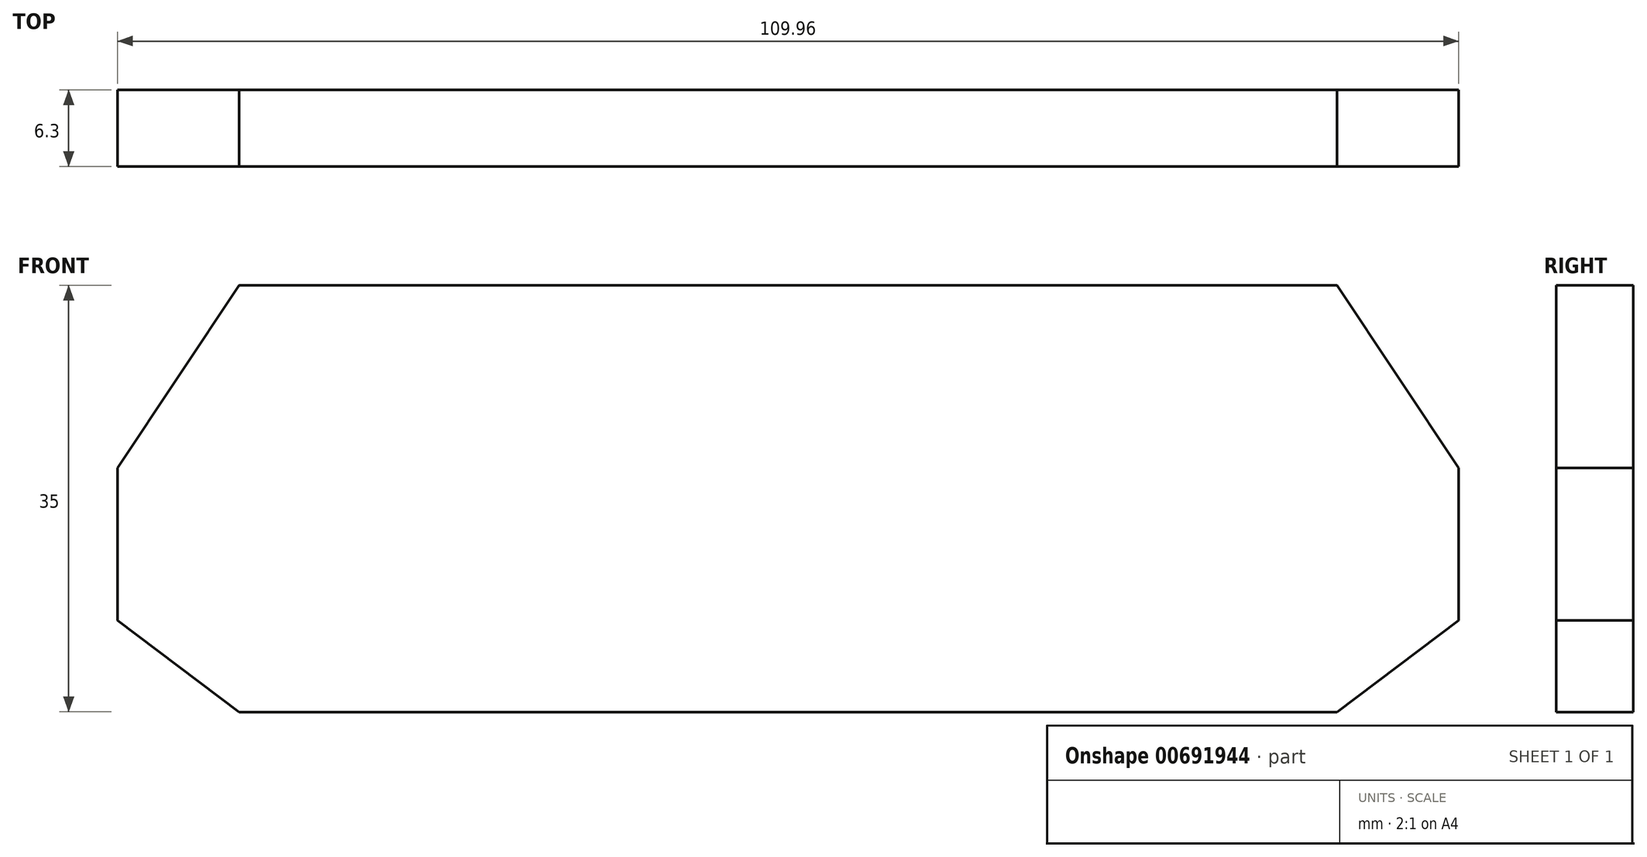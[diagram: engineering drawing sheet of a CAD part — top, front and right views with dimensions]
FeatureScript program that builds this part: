
annotation { "Feature Type Name" : "Feature", "Feature Type Description" : "" }
export const myFeature = defineFeature(function(context is Context, id is Id, definition is map)
    precondition{}
    {
        {
            var Q0;
            Q0=qCreatedBy(makeId("Front.planeOp"),FACE);
            var sketch = newSketch(context, id + "F0", { "sketchPlane" : qUnion([Q0])});
            skLineSegment(sketch, "E0", {"start": v(45, 48.44) * mm, "end": v(54.98, 33.46) * mm});
            skLineSegment(sketch, "E1", {"start": v(54.98, 33.46) * mm, "end": v(54.98, 20.96) * mm});
            skLineSegment(sketch, "E2", {"start": v(54.98, 20.96) * mm, "end": v(45, 13.44) * mm});
            skLineSegment(sketch, "E3", {"start": v(45, 13.44) * mm, "end": v(0, 13.44) * mm});
            skLineSegment(sketch, "E4", {"start": v(45, 48.44) * mm, "end": v(0, 48.44) * mm});
            skLineSegment(sketch, "E5", {"start": v(0, 48.44) * mm, "end": v(0, 13.44) * mm});
            skLineSegment(sketch, "E6.MirrorCS", {"start": v(-45, 48.44) * mm, "end": v(0, 48.44) * mm});
            skLineSegment(sketch, "E7.MirrorCS", {"start": v(-45, 48.44) * mm, "end": v(-54.98, 33.46) * mm});
            skLineSegment(sketch, "E8.MirrorCS", {"start": v(-54.98, 33.46) * mm, "end": v(-54.98, 20.96) * mm});
            skLineSegment(sketch, "E9.MirrorCS", {"start": v(-54.98, 20.96) * mm, "end": v(-45, 13.44) * mm});
            skLineSegment(sketch, "E10.MirrorCS", {"start": v(-45, 13.44) * mm, "end": v(0, 13.44) * mm});
            skSolve(sketch);
        }
        {
            var Q0;
            Q0 = qSketchRegion(id + "F0", true);
            extrude(context, id + "F1", {"entities" : qUnion([Q0]), "depth" : 6.3 * mm, "offsetDistance" : 25.4 * mm});
        }
    });
